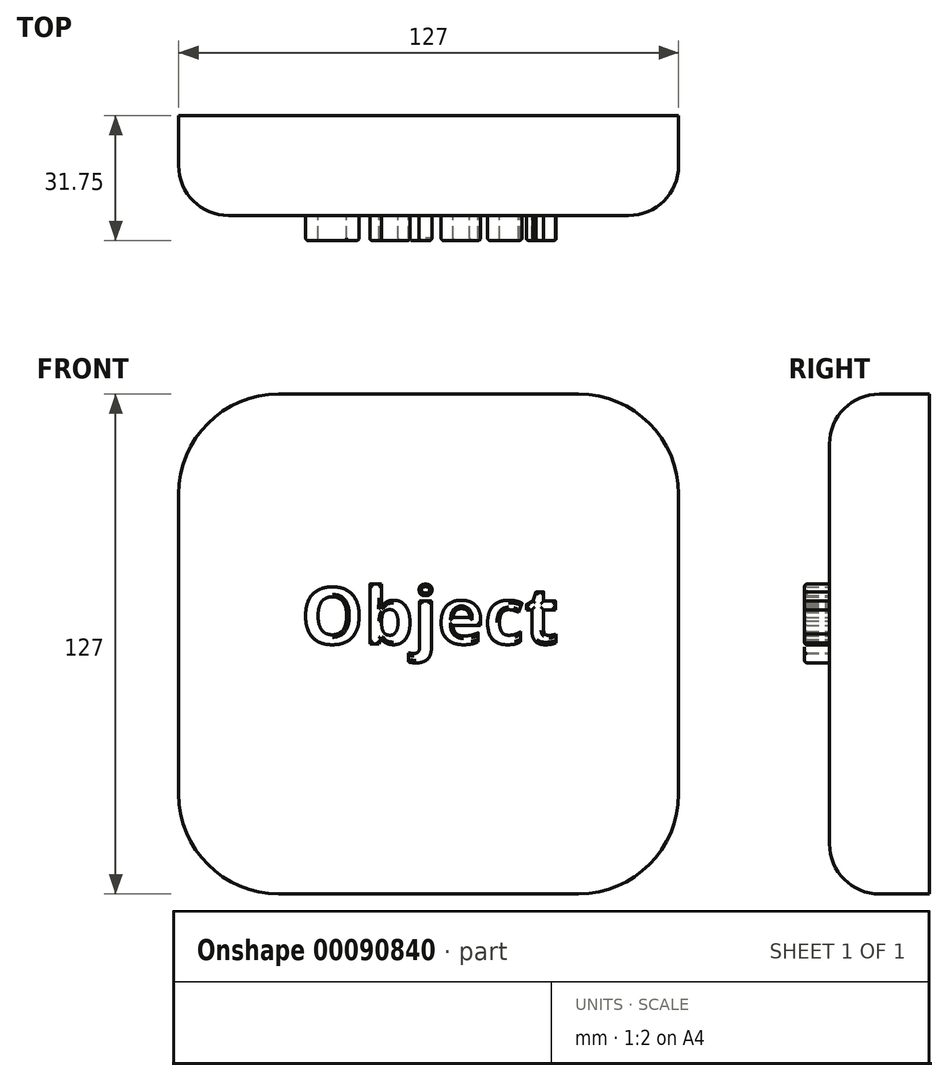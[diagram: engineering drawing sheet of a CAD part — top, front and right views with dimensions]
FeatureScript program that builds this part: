
annotation { "Feature Type Name" : "Feature", "Feature Type Description" : "" }
export const myFeature = defineFeature(function(context is Context, id is Id, definition is map)
    precondition{}
    {
        {
            var Q0;
            Q0=qCreatedBy(makeId("Front.planeOp"),FACE);
            var sketch = newSketch(context, id + "F0", { "sketchPlane" : qUnion([Q0])});
            skLineSegment(sketch, "E0.bottom", {"start": v(63.5, -63.5) * mm, "end": v(-63.5, -63.5) * mm});
            skLineSegment(sketch, "E0.top", {"start": v(63.5, 63.5) * mm, "end": v(-63.5, 63.5) * mm});
            skLineSegment(sketch, "E0.left", {"start": v(63.5, -63.5) * mm, "end": v(63.5, 63.5) * mm});
            skLineSegment(sketch, "E0.right", {"start": v(-63.5, -63.5) * mm, "end": v(-63.5, 63.5) * mm});
            skPoint(sketch, "E0.middle", {"position": v(0, 0) * mm});
            skSolve(sketch);
        }
        {
            var Q0;
            Q0=makeQuery(id+"F0.imprint","IMPRINT",FACE,{"disambiguationData":[TD([[makeQuery(id+"F0.imprint","IMPRINT",EDGE,{"derivedFrom":sQuery(id+"F0.wireOp",EDGE,"E0.bottom")}),-1.0]])]});
            extrude(context, id + "F1", {"entities" : qUnion([Q0]), "oppositeDirection" : true, "depth" : 25.4 * mm});
        }
        {
            var Q0;
            Q0=makeQuery(id+"F1.opExtrude","CAP_FACE",FACE,{"disambiguationData":[OSD([sQuery(id+"F0.wireOp",EDGE,"E0.bottom"),sQuery(id+"F0.wireOp",EDGE,"E0.top"),sQuery(id+"F0.wireOp",EDGE,"E0.left"),sQuery(id+"F0.wireOp",EDGE,"E0.right")])],"isStart":true});
            var sketch = newSketch(context, id + "F2", { "sketchPlane" : qUnion([Q0])});
            skText(sketch, "E1", { "text": "Object", "fontName": "OpenSans-Bold.ttf"});
            const initialGuessF2  = {"E1": [-0.03242, 0, 1, 0, 0.0144]};
            skSetInitialGuess(sketch, initialGuessF2);
            skSolve(sketch);
        }
        {
            var Q0;
            Q0 = qSketchRegion(id + "F2", true);
            extrude(context, id + "F3", {"entities" : qUnion([Q0]), "operationType" : NewBodyOperationType.ADD, "depth" : 6.35 * mm});
        }
        {
            var Q0;
            Q0=makeQuery(id+"F1.opExtrude","SWEPT_EDGE",EDGE,{"disambiguationData":[OSD([sQuery(id+"F0.wireOp",EDGE,"E0.bottom"),sQuery(id+"F0.wireOp",EDGE,"E0.right")])]});
            var Q1;
            Q1=makeQuery(id+"F1.opExtrude","SWEPT_EDGE",EDGE,{"disambiguationData":[OSD([sQuery(id+"F0.wireOp",EDGE,"E0.top"),sQuery(id+"F0.wireOp",EDGE,"E0.left")])]});
            var Q2;
            Q2=makeQuery(id+"F1.opExtrude","SWEPT_EDGE",EDGE,{"disambiguationData":[OSD([sQuery(id+"F0.wireOp",EDGE,"E0.bottom"),sQuery(id+"F0.wireOp",EDGE,"E0.left")])]});
            var Q3;
            Q3=makeQuery(id+"F1.opExtrude","SWEPT_EDGE",EDGE,{"disambiguationData":[OSD([sQuery(id+"F0.wireOp",EDGE,"E0.top"),sQuery(id+"F0.wireOp",EDGE,"E0.right")])]});
            fillet(context, id + "F4", {"entities" : qUnion([Q0, Q1, Q2, Q3]), "radius" : 25.4 * mm, "tangentPropagation" : true, "allowEdgeOverflow" : false});
        }
        {
            var Q0;
            Q0=makeQuery(id+"F1.opExtrude","CAP_EDGE",EDGE,{"disambiguationData":[OSD([sQuery(id+"F0.wireOp",EDGE,"E0.left")])],"isStart":true});
            fillet(context, id + "F5", {"entities" : qUnion([Q0]), "radius" : 12.7 * mm, "tangentPropagation" : true, "allowEdgeOverflow" : false});
        }
        {
            var Q0;
            Q0=makeQuery(id+"F3.opExtrude","CAP_FACE",FACE,{"disambiguationData":[OSD([sQuery(id+"F2.wireOp",EDGE,"E1.sketch_text.stroke-72"),sQuery(id+"F2.wireOp",EDGE,"E1.sketch_text.stroke-73"),sQuery(id+"F2.wireOp",EDGE,"E1.sketch_text.stroke-74"),sQuery(id+"F2.wireOp",EDGE,"E1.sketch_text.stroke-75"),sQuery(id+"F2.wireOp",EDGE,"E1.sketch_text.stroke-76"),sQuery(id+"F2.wireOp",EDGE,"E1.sketch_text.stroke-77"),sQuery(id+"F2.wireOp",EDGE,"E1.sketch_text.stroke-78"),sQuery(id+"F2.wireOp",EDGE,"E1.sketch_text.stroke-79"),sQuery(id+"F2.wireOp",EDGE,"E1.sketch_text.stroke-80"),sQuery(id+"F2.wireOp",EDGE,"E1.sketch_text.stroke-81"),sQuery(id+"F2.wireOp",EDGE,"E1.sketch_text.stroke-82"),sQuery(id+"F2.wireOp",EDGE,"E1.sketch_text.stroke-83"),sQuery(id+"F2.wireOp",EDGE,"E1.sketch_text.stroke-84"),sQuery(id+"F2.wireOp",EDGE,"E1.sketch_text.stroke-85")])],"isStart":false});
            var Q1;
            Q1=makeQuery(id+"F3.opExtrude","CAP_FACE",FACE,{"disambiguationData":[OSD([sQuery(id+"F2.wireOp",EDGE,"E1.sketch_text.stroke-52"),sQuery(id+"F2.wireOp",EDGE,"E1.sketch_text.stroke-53"),sQuery(id+"F2.wireOp",EDGE,"E1.sketch_text.stroke-54"),sQuery(id+"F2.wireOp",EDGE,"E1.sketch_text.stroke-55"),sQuery(id+"F2.wireOp",EDGE,"E1.sketch_text.stroke-56"),sQuery(id+"F2.wireOp",EDGE,"E1.sketch_text.stroke-57"),sQuery(id+"F2.wireOp",EDGE,"E1.sketch_text.stroke-58"),sQuery(id+"F2.wireOp",EDGE,"E1.sketch_text.stroke-59"),sQuery(id+"F2.wireOp",EDGE,"E1.sketch_text.stroke-60"),sQuery(id+"F2.wireOp",EDGE,"E1.sketch_text.stroke-61"),sQuery(id+"F2.wireOp",EDGE,"E1.sketch_text.stroke-62"),sQuery(id+"F2.wireOp",EDGE,"E1.sketch_text.stroke-63"),sQuery(id+"F2.wireOp",EDGE,"E1.sketch_text.stroke-64"),sQuery(id+"F2.wireOp",EDGE,"E1.sketch_text.stroke-65"),sQuery(id+"F2.wireOp",EDGE,"E1.sketch_text.stroke-66"),sQuery(id+"F2.wireOp",EDGE,"E1.sketch_text.stroke-67"),sQuery(id+"F2.wireOp",EDGE,"E1.sketch_text.stroke-68"),sQuery(id+"F2.wireOp",EDGE,"E1.sketch_text.stroke-69"),sQuery(id+"F2.wireOp",EDGE,"E1.sketch_text.stroke-70"),sQuery(id+"F2.wireOp",EDGE,"E1.sketch_text.stroke-71")])],"isStart":false});
            var Q2;
            Q2=makeQuery(id+"F3.opExtrude","CAP_FACE",FACE,{"disambiguationData":[OSD([sQuery(id+"F2.wireOp",EDGE,"E1.sketch_text.stroke-86"),sQuery(id+"F2.wireOp",EDGE,"E1.sketch_text.stroke-87"),sQuery(id+"F2.wireOp",EDGE,"E1.sketch_text.stroke-88"),sQuery(id+"F2.wireOp",EDGE,"E1.sketch_text.stroke-89"),sQuery(id+"F2.wireOp",EDGE,"E1.sketch_text.stroke-90"),sQuery(id+"F2.wireOp",EDGE,"E1.sketch_text.stroke-91"),sQuery(id+"F2.wireOp",EDGE,"E1.sketch_text.stroke-92"),sQuery(id+"F2.wireOp",EDGE,"E1.sketch_text.stroke-93"),sQuery(id+"F2.wireOp",EDGE,"E1.sketch_text.stroke-94"),sQuery(id+"F2.wireOp",EDGE,"E1.sketch_text.stroke-95"),sQuery(id+"F2.wireOp",EDGE,"E1.sketch_text.stroke-96"),sQuery(id+"F2.wireOp",EDGE,"E1.sketch_text.stroke-97"),sQuery(id+"F2.wireOp",EDGE,"E1.sketch_text.stroke-98"),sQuery(id+"F2.wireOp",EDGE,"E1.sketch_text.stroke-99"),sQuery(id+"F2.wireOp",EDGE,"E1.sketch_text.stroke-100"),sQuery(id+"F2.wireOp",EDGE,"E1.sketch_text.stroke-101"),sQuery(id+"F2.wireOp",EDGE,"E1.sketch_text.stroke-102"),sQuery(id+"F2.wireOp",EDGE,"E1.sketch_text.stroke-103")])],"isStart":false});
            var Q3;
            Q3=makeQuery(id+"F3.opExtrude","CAP_FACE",FACE,{"disambiguationData":[OSD([sQuery(id+"F2.wireOp",EDGE,"E1.sketch_text.stroke-37"),sQuery(id+"F2.wireOp",EDGE,"E1.sketch_text.stroke-38"),sQuery(id+"F2.wireOp",EDGE,"E1.sketch_text.stroke-39"),sQuery(id+"F2.wireOp",EDGE,"E1.sketch_text.stroke-40"),sQuery(id+"F2.wireOp",EDGE,"E1.sketch_text.stroke-41"),sQuery(id+"F2.wireOp",EDGE,"E1.sketch_text.stroke-42"),sQuery(id+"F2.wireOp",EDGE,"E1.sketch_text.stroke-43"),sQuery(id+"F2.wireOp",EDGE,"E1.sketch_text.stroke-44"),sQuery(id+"F2.wireOp",EDGE,"E1.sketch_text.stroke-45"),sQuery(id+"F2.wireOp",EDGE,"E1.sketch_text.stroke-46")])],"isStart":false});
            var Q4;
            Q4=makeQuery(id+"F3.opExtrude","CAP_FACE",FACE,{"disambiguationData":[OSD([sQuery(id+"F2.wireOp",EDGE,"E1.sketch_text.stroke-14"),sQuery(id+"F2.wireOp",EDGE,"E1.sketch_text.stroke-15"),sQuery(id+"F2.wireOp",EDGE,"E1.sketch_text.stroke-16"),sQuery(id+"F2.wireOp",EDGE,"E1.sketch_text.stroke-17"),sQuery(id+"F2.wireOp",EDGE,"E1.sketch_text.stroke-18"),sQuery(id+"F2.wireOp",EDGE,"E1.sketch_text.stroke-19"),sQuery(id+"F2.wireOp",EDGE,"E1.sketch_text.stroke-20"),sQuery(id+"F2.wireOp",EDGE,"E1.sketch_text.stroke-21"),sQuery(id+"F2.wireOp",EDGE,"E1.sketch_text.stroke-22"),sQuery(id+"F2.wireOp",EDGE,"E1.sketch_text.stroke-23"),sQuery(id+"F2.wireOp",EDGE,"E1.sketch_text.stroke-24"),sQuery(id+"F2.wireOp",EDGE,"E1.sketch_text.stroke-25"),sQuery(id+"F2.wireOp",EDGE,"E1.sketch_text.stroke-26"),sQuery(id+"F2.wireOp",EDGE,"E1.sketch_text.stroke-27"),sQuery(id+"F2.wireOp",EDGE,"E1.sketch_text.stroke-28"),sQuery(id+"F2.wireOp",EDGE,"E1.sketch_text.stroke-29"),sQuery(id+"F2.wireOp",EDGE,"E1.sketch_text.stroke-30"),sQuery(id+"F2.wireOp",EDGE,"E1.sketch_text.stroke-31"),sQuery(id+"F2.wireOp",EDGE,"E1.sketch_text.stroke-32"),sQuery(id+"F2.wireOp",EDGE,"E1.sketch_text.stroke-33"),sQuery(id+"F2.wireOp",EDGE,"E1.sketch_text.stroke-34"),sQuery(id+"F2.wireOp",EDGE,"E1.sketch_text.stroke-35"),sQuery(id+"F2.wireOp",EDGE,"E1.sketch_text.stroke-36")])],"isStart":false});
            var Q5;
            Q5=makeQuery(id+"F3.opExtrude","CAP_FACE",FACE,{"disambiguationData":[OSD([sQuery(id+"F2.wireOp",EDGE,"E1.sketch_text.stroke-47"),sQuery(id+"F2.wireOp",EDGE,"E1.sketch_text.stroke-48"),sQuery(id+"F2.wireOp",EDGE,"E1.sketch_text.stroke-49"),sQuery(id+"F2.wireOp",EDGE,"E1.sketch_text.stroke-50"),sQuery(id+"F2.wireOp",EDGE,"E1.sketch_text.stroke-51")])],"isStart":false});
            var Q6;
            Q6=makeQuery(id+"F3.opExtrude","CAP_FACE",FACE,{"disambiguationData":[OSD([sQuery(id+"F2.wireOp",EDGE,"E1.sketch_text.stroke-0"),sQuery(id+"F2.wireOp",EDGE,"E1.sketch_text.stroke-1"),sQuery(id+"F2.wireOp",EDGE,"E1.sketch_text.stroke-2"),sQuery(id+"F2.wireOp",EDGE,"E1.sketch_text.stroke-3"),sQuery(id+"F2.wireOp",EDGE,"E1.sketch_text.stroke-4"),sQuery(id+"F2.wireOp",EDGE,"E1.sketch_text.stroke-5"),sQuery(id+"F2.wireOp",EDGE,"E1.sketch_text.stroke-6"),sQuery(id+"F2.wireOp",EDGE,"E1.sketch_text.stroke-7"),sQuery(id+"F2.wireOp",EDGE,"E1.sketch_text.stroke-8"),sQuery(id+"F2.wireOp",EDGE,"E1.sketch_text.stroke-9"),sQuery(id+"F2.wireOp",EDGE,"E1.sketch_text.stroke-10"),sQuery(id+"F2.wireOp",EDGE,"E1.sketch_text.stroke-11"),sQuery(id+"F2.wireOp",EDGE,"E1.sketch_text.stroke-12"),sQuery(id+"F2.wireOp",EDGE,"E1.sketch_text.stroke-13")])],"isStart":false});
            fillet(context, id + "F6", {"entities" : qUnion([Q0, Q1, Q2, Q3, Q4, Q5, Q6]), "radius" : 0.64 * mm, "tangentPropagation" : true, "allowEdgeOverflow" : false});
        }
        {
            var Q0;
            Q0=qCreatedBy(makeId("Right.planeOp"),FACE);
            var sketch = newSketch(context, id + "F7", { "sketchPlane" : qUnion([Q0])});
            skCircle(sketch, "E2", {"center": v(12.7, 63.5) * mm, "radius": 0.64 * mm});
            skSolve(sketch);
        }
        {
            var Q0;
            Q0=qCreatedBy(makeId("Front.planeOp"),FACE);
            var Q1;
            Q1=sQuery(id+"F7.wireOp",VERTEX,"E2.center");
            cPlane(context, id + "F8", {"entities" : qUnion([Q0, Q1]), "cplaneType" : CPlaneType.PLANE_POINT, "offset" : 152.4 * mm, "width" : 152.4 * mm, "height" : 152.4 * mm});
        }
    });
